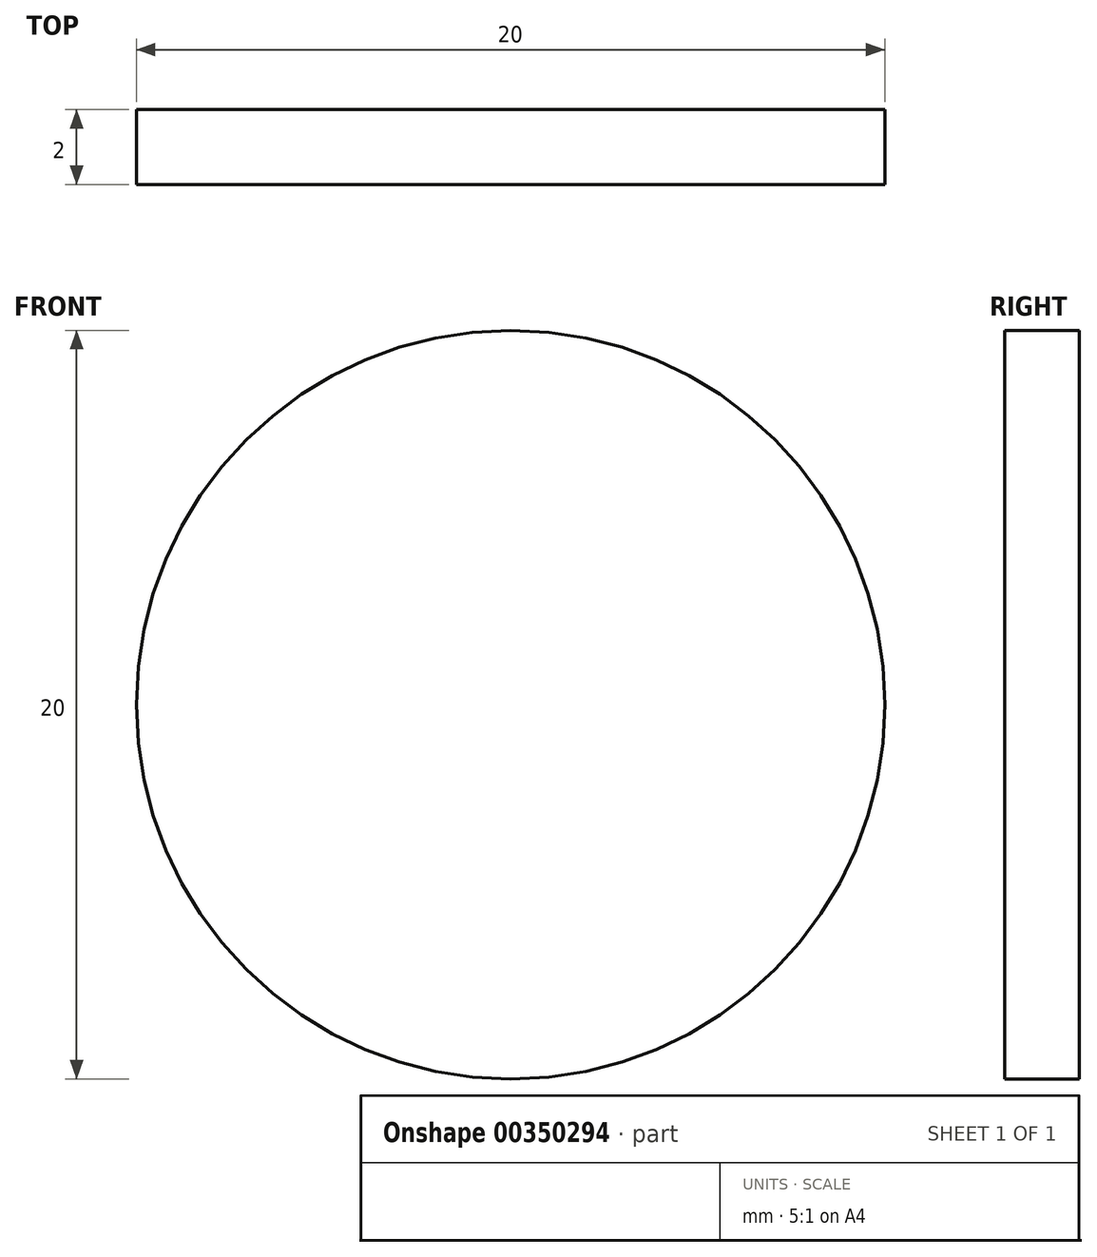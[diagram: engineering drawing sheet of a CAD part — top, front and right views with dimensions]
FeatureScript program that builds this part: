
annotation { "Feature Type Name" : "Feature", "Feature Type Description" : "" }
export const myFeature = defineFeature(function(context is Context, id is Id, definition is map)
    precondition{}
    {
        {
            var Q0;
            Q0=qCreatedBy(makeId("Front.planeOp"),FACE);
            var sketch = newSketch(context, id + "F0", { "sketchPlane" : qUnion([Q0])});
            skCircle(sketch, "E0", {"center": v(0, 0) * mm, "radius": 10 * mm});
            skSolve(sketch);
        }
        {
            var Q0;
            Q0=makeQuery(id+"F0.imprint","IMPRINT",FACE,{"disambiguationData":[TD([[makeQuery(id+"F0.imprint","IMPRINT",EDGE,{"derivedFrom":sQuery(id+"F0.wireOp",EDGE,"E0")}),1.0]])]});
            extrude(context, id + "F1", {"entities" : qUnion([Q0]), "depth" : 2 * mm});
        }
    });
